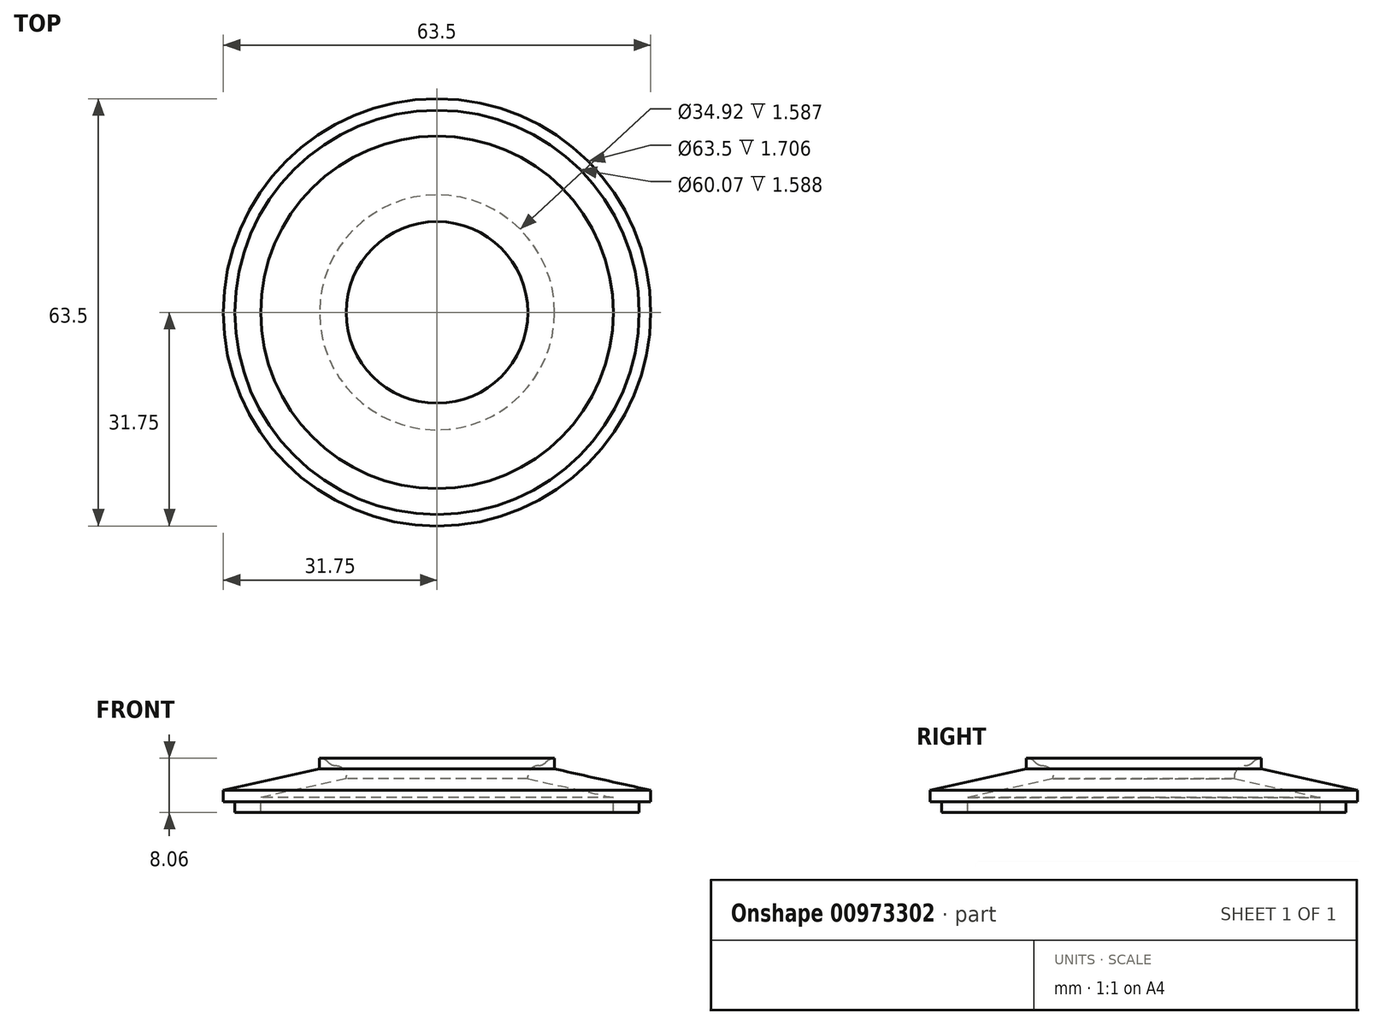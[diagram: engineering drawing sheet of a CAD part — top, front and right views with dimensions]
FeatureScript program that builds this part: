
annotation { "Feature Type Name" : "Feature", "Feature Type Description" : "" }
export const myFeature = defineFeature(function(context is Context, id is Id, definition is map)
    precondition{}
    {
        {
            var Q0;
            Q0=qCreatedBy(makeId("Front.planeOp"),FACE);
            var sketch = newSketch(context, id + "F0", { "sketchPlane" : qUnion([Q0])});
            skLineSegment(sketch, "E0", {"start": v(0, 0) * mm, "end": v(0, 53.06) * mm, "construction": true});
            skLineSegment(sketch, "E1", {"start": v(4.76, 0) * mm, "end": v(4.76, 1.59) * mm, "construction": true});
            skLineSegment(sketch, "E2", {"start": v(4.76, 0) * mm, "end": v(15.88, 0) * mm, "construction": true});
            skLineSegment(sketch, "E3", {"start": v(4.76, 1.59) * mm, "end": v(26.2, 1.59) * mm, "construction": true});
            skLineSegment(sketch, "E4.0", {"start": v(13.5, 16.08) * mm, "end": v(13.5, 13.75) * mm});
            skLineSegment(sketch, "E5.0", {"start": v(31.75, 12.02) * mm, "end": v(17.46, 15.2) * mm});
            skLineSegment(sketch, "E6", {"start": v(26.2, 3.97) * mm, "end": v(26.2, 1.59) * mm, "construction": true});
            skLineSegment(sketch, "E7", {"start": v(26.2, 3.97) * mm, "end": v(31.75, 3.97) * mm, "construction": true});
            skLineSegment(sketch, "E8", {"start": v(26.2, 10.93) * mm, "end": v(26.2, 8.73) * mm});
            skLineSegment(sketch, "E9", {"start": v(26.2, 8.73) * mm, "end": v(30.04, 8.73) * mm});
            skLineSegment(sketch, "E10.trimOffspring", {"start": v(26.2, 10.93) * mm, "end": v(13.5, 13.75) * mm});
            skLineSegment(sketch, "E11", {"start": v(15.88, 15.55) * mm, "end": v(15.88, 16.79) * mm});
            skLineSegment(sketch, "E12", {"start": v(17.46, 19.85) * mm, "end": v(11.11, 19.85) * mm, "construction": true});
            skLineSegment(sketch, "E13", {"start": v(11.11, 19.85) * mm, "end": v(11.11, 21.44) * mm, "construction": true});
            skLineSegment(sketch, "E14", {"start": v(17.46, 24.61) * mm, "end": v(17.46, 18.26) * mm, "construction": true});
            skLineSegment(sketch, "E15.trimOffspring", {"start": v(15.88, 15.55) * mm, "end": v(13.5, 16.08) * mm});
            skLineSegment(sketch, "E16", {"start": v(17.46, 24.61) * mm, "end": v(28.58, 24.61) * mm, "construction": true});
            skLineSegment(sketch, "E17", {"start": v(28.58, 24.61) * mm, "end": v(28.58, 27.79) * mm, "construction": true});
            skLineSegment(sketch, "E18", {"start": v(28.58, 27.79) * mm, "end": v(15.88, 27.79) * mm, "construction": true});
            skLineSegment(sketch, "E19", {"start": v(15.87, 27.79) * mm, "end": v(15.87, 21.44) * mm, "construction": true});
            skLineSegment(sketch, "E20", {"start": v(15.88, 21.44) * mm, "end": v(11.11, 21.44) * mm, "construction": true});
            skLineSegment(sketch, "E21", {"start": v(31.75, 12.02) * mm, "end": v(31.75, 10.32) * mm});
            skLineSegment(sketch, "E22", {"start": v(31.75, 3.97) * mm, "end": v(31.75, 0) * mm, "construction": true});
            skLineSegment(sketch, "E23", {"start": v(15.88, 0) * mm, "end": v(15.88, -4.76) * mm, "construction": true});
            skLineSegment(sketch, "E24", {"start": v(15.88, -4.76) * mm, "end": v(11.11, -4.76) * mm, "construction": true});
            skLineSegment(sketch, "E25", {"start": v(11.11, -4.76) * mm, "end": v(11.11, -6.35) * mm, "construction": true});
            skLineSegment(sketch, "E26.trimOffspring", {"start": v(17.46, 0) * mm, "end": v(31.75, 0) * mm, "construction": true});
            skLineSegment(sketch, "E27", {"start": v(11.11, -6.35) * mm, "end": v(19.94, -6.35) * mm, "construction": true});
            skLineSegment(sketch, "E28", {"start": v(19.94, -19.05) * mm, "end": v(21.53, -19.05) * mm, "construction": true});
            skLineSegment(sketch, "E29", {"start": v(19.94, -19.05) * mm, "end": v(19.94, -6.35) * mm, "construction": true});
            skLineSegment(sketch, "E30", {"start": v(17.46, 0) * mm, "end": v(17.46, -4.76) * mm, "construction": true});
            skLineSegment(sketch, "E31", {"start": v(17.46, -4.76) * mm, "end": v(21.53, -4.76) * mm, "construction": true});
            skLineSegment(sketch, "E32", {"start": v(21.53, -4.76) * mm, "end": v(21.53, -19.05) * mm, "construction": true});
            skLineSegment(sketch, "E33", {"start": v(15.88, 16.79) * mm, "end": v(17.46, 16.79) * mm});
            skLineSegment(sketch, "E34.trimOffspring", {"start": v(17.46, 16.79) * mm, "end": v(17.46, 15.2) * mm});
            skPoint(sketch, "E35.orphan", {"position": v(30.16, 3.97) * mm});
            skLineSegment(sketch, "E36", {"start": v(31.75, 10.32) * mm, "end": v(30.04, 10.32) * mm});
            skLineSegment(sketch, "E37", {"start": v(30.04, 10.32) * mm, "end": v(30.04, 8.73) * mm});
            skPoint(sketch, "E38.orphan", {"position": v(11.9, 14.1) * mm});
            skPoint(sketch, "E39.orphan", {"position": v(15.88, 19.85) * mm});
            skSolve(sketch);
        }
        {
            var Q0;
            Q0=qConstructionFilter(qBodyType(qCreatedBy(id+"F0",EDGE),BodyType.WIRE),ConstructionObject.NO);
            var Q1;
            Q1=sQuery(id+"F0.wireOp",EDGE,"E0");
            revolve(context, id + "F1", {"bodyType" : ToolBodyType.SURFACE, "surfaceOperationType" : NewSurfaceOperationType.NEW, "surfaceEntities" : qUnion([Q0]), "axis" : qUnion([Q1]), "revolveType" : RevolveType.FULL});
        }
        {
            var Q0;
            Q0=makeQuery(id+"F1.opRevolve","SWEPT_EDGE",EDGE,{"disambiguationData":[OSD([sQuery(id+"F0.wireOp",VERTEX,"E15.trimOffspring.end")])]});
            fillet(context, id + "F2", {"entities" : qUnion([Q0]), "radius" : 1.59 * mm, "tangentPropagation" : true, "allowEdgeOverflow" : false});
        }
        {
            var Q0;
            Q0=makeQuery(id+"F1.opRevolve","SWEPT_EDGE",EDGE,{"disambiguationData":[OSD([sQuery(id+"F0.wireOp",VERTEX,"E33.start")])]});
            fillet(context, id + "F3", {"entities" : qUnion([Q0]), "radius" : 1.59 * mm, "tangentPropagation" : true, "allowEdgeOverflow" : false});
        }
        {
            var Q0;
            Q0=makeQuery(id+"F3.opFillet","BLEND_EDGE",EDGE,{"blendedFrom":[makeQuery(id+"F1.opRevolve","SWEPT_EDGE",EDGE,{"disambiguationData":[OSD([sQuery(id+"F0.wireOp",VERTEX,"E33.start")])]}),makeQuery(id+"F1.opRevolve","SWEPT_FACE",FACE,{"disambiguationData":[OSD([sQuery(id+"F0.wireOp",EDGE,"E15.trimOffspring")])]})],"blendedInto":[makeQuery(id+"F1.opRevolve","SWEPT_FACE",FACE,{"disambiguationData":[OSD([sQuery(id+"F0.wireOp",EDGE,"E15.trimOffspring")])]})]});
            fillet(context, id + "F4", {"entities" : qUnion([Q0]), "radius" : 1.59 * mm, "tangentPropagation" : true, "allowEdgeOverflow" : false});
        }
    });
